# Revit family: Window_Vinyl_Atrium-SilentGuard_7100-SH
name_source: partatom
category: Windows
units: mm (PartAtom-declared; Revit-internal decimal feet)

## family parameters
Always vertical = Yes
Classification Number = 23.30.20.17.17.11
Cut with Voids When Loaded = No
Host = Wall
Room Calculation Point = No
Shared = No

## types (1)
- Window_Vinyl_Atrium-SilentGuard_7100-SH
    Air Infiltration = as Specified
    Assembly Code = B2020100
    Construction Details = http://www.silent-guard.com
    Description = as Specified
    Expected Lifespan (Years) = 0
    Forced Entry Rating = as Specified
    Frame Thickness = 0' - 4 1/2"
    Glass Thickness = 0' - 1"
    Green Building-LEED = http://www.arcat.com
    Height = 3' - 11 1/2"
    Keynote = as Specified
    Maintenance Schedule (Months) = 0
    Manufacturer = Atrium Companies, Inc.
    Manufacturer Fax = 214-630-5010
    Manufacturer Website = http://www.silent-guard.com
    Meets Egress = as Specified
    Miami Dade Conformance = as Specified
    Model = as Specified
    Product Data = http://www.arcat.com
    RO Spacing_Bottom = 0' - 0 1/4"
    RO Spacing_Sides = 0' - 0 1/4"
    RO Spacing_Top = 0' - 0 1/4"
    Rough Height = 4' - 0"
    Rough Width = 2' - 6"
    Sales Information = http://www.silent-guard.com
    Send Message = http://www.arcat.com Email
    Standards Conformance = as Specified
    Structural Test Pressure = as Specified
    Test Data = http://www.silent-guard.com
    URL = http://www.silent-guard.com
    Wall Closure = By host
    Warranty Duration (Years) = 0
    Water Penetration = as Specified
    Width = 2' - 5 1/2"

## geometry (parser evidence)
native form markers: Blend x10, Sweep x9
no freeform markers — native parametric forms only
